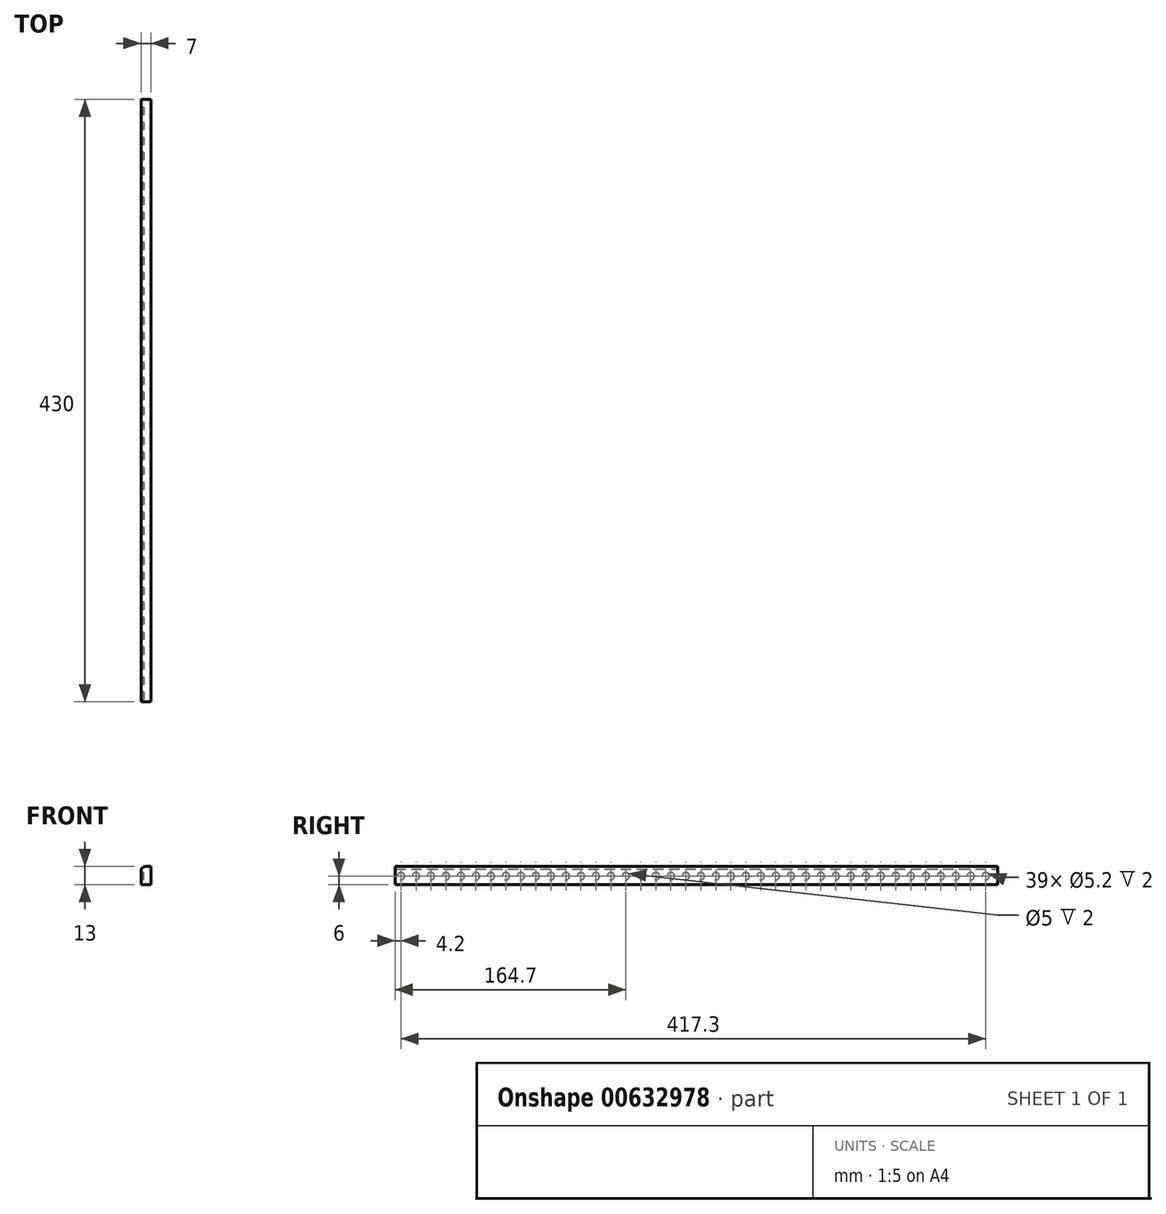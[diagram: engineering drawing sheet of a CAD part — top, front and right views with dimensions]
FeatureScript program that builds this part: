
annotation { "Feature Type Name" : "Feature", "Feature Type Description" : "" }
export const myFeature = defineFeature(function(context is Context, id is Id, definition is map)
    precondition{}
    {
        {
            var Q0;
            Q0=qCreatedBy(makeId("Right.planeOp"),FACE);
            var sketch = newSketch(context, id + "F0", { "sketchPlane" : qUnion([Q0])});
            skLineSegment(sketch, "E0.bottom", {"start": v(215, 7) * mm, "end": v(-215, 7) * mm});
            skLineSegment(sketch, "E0.top", {"start": v(215, -6) * mm, "end": v(-215, -6) * mm});
            skLineSegment(sketch, "E0.left", {"start": v(215, 7) * mm, "end": v(215, -6) * mm});
            skLineSegment(sketch, "E0.right", {"start": v(-215, 7) * mm, "end": v(-215, -6) * mm});
            skLineSegment(sketch, "E1", {"start": v(215, 0) * mm, "end": v(-215, 0) * mm, "construction": true});
            skCircle(sketch, "E2", {"center": v(206.5, 0) * mm, "radius": 2.6 * mm});
            skCircle(sketch, "E3", {"center": v(195.8, 0) * mm, "radius": 2.6 * mm});
            skCircle(sketch, "E4", {"center": v(185.1, 0) * mm, "radius": 2.6 * mm});
            skCircle(sketch, "E5", {"center": v(174.4, 0) * mm, "radius": 2.6 * mm});
            skCircle(sketch, "E6", {"center": v(163.7, 0) * mm, "radius": 2.6 * mm});
            skCircle(sketch, "E7", {"center": v(153, 0) * mm, "radius": 2.6 * mm});
            skCircle(sketch, "E8", {"center": v(142.3, 0) * mm, "radius": 2.6 * mm});
            skCircle(sketch, "E9", {"center": v(131.6, 0) * mm, "radius": 2.6 * mm});
            skCircle(sketch, "E10", {"center": v(120.9, 0) * mm, "radius": 2.6 * mm});
            skCircle(sketch, "E11", {"center": v(110.2, 0) * mm, "radius": 2.6 * mm});
            skCircle(sketch, "E12", {"center": v(99.5, 0) * mm, "radius": 2.6 * mm});
            skCircle(sketch, "E13", {"center": v(88.8, 0) * mm, "radius": 2.6 * mm});
            skCircle(sketch, "E14", {"center": v(78.1, 0) * mm, "radius": 2.6 * mm});
            skCircle(sketch, "E15", {"center": v(67.4, 0) * mm, "radius": 2.6 * mm});
            skCircle(sketch, "E16", {"center": v(56.7, 0) * mm, "radius": 2.6 * mm});
            skCircle(sketch, "E17", {"center": v(46, 0) * mm, "radius": 2.6 * mm});
            skCircle(sketch, "E18", {"center": v(35.3, 0) * mm, "radius": 2.6 * mm});
            skCircle(sketch, "E19", {"center": v(24.6, 0) * mm, "radius": 2.6 * mm});
            skCircle(sketch, "E20", {"center": v(13.9, 0) * mm, "radius": 2.6 * mm});
            skCircle(sketch, "E21", {"center": v(3.2, 0) * mm, "radius": 2.6 * mm});
            skCircle(sketch, "E22", {"center": v(-7.5, 0) * mm, "radius": 2.6 * mm});
            skCircle(sketch, "E23", {"center": v(-18.2, 0) * mm, "radius": 2.6 * mm});
            skCircle(sketch, "E24", {"center": v(-28.9, 0) * mm, "radius": 2.6 * mm});
            skCircle(sketch, "E25", {"center": v(-39.6, 0) * mm, "radius": 2.6 * mm});
            skCircle(sketch, "E26", {"center": v(-50.3, 0) * mm, "radius": 2.5 * mm});
            skCircle(sketch, "E27", {"center": v(-61, 0) * mm, "radius": 2.6 * mm});
            skCircle(sketch, "E28", {"center": v(-71.7, 0) * mm, "radius": 2.6 * mm});
            skCircle(sketch, "E29", {"center": v(-82.4, 0) * mm, "radius": 2.6 * mm});
            skCircle(sketch, "E30", {"center": v(-93.1, 0) * mm, "radius": 2.6 * mm});
            skCircle(sketch, "E31", {"center": v(-103.8, 0) * mm, "radius": 2.6 * mm});
            skCircle(sketch, "E32", {"center": v(-114.5, 0) * mm, "radius": 2.6 * mm});
            skCircle(sketch, "E33", {"center": v(-125.2, 0) * mm, "radius": 2.6 * mm});
            skCircle(sketch, "E34", {"center": v(-135.9, 0) * mm, "radius": 2.6 * mm});
            skCircle(sketch, "E35", {"center": v(-146.6, 0) * mm, "radius": 2.6 * mm});
            skCircle(sketch, "E36", {"center": v(-157.3, 0) * mm, "radius": 2.6 * mm});
            skCircle(sketch, "E37", {"center": v(-168, 0) * mm, "radius": 2.6 * mm});
            skCircle(sketch, "E38", {"center": v(-178.7, 0) * mm, "radius": 2.6 * mm});
            skCircle(sketch, "E39", {"center": v(-189.4, 0) * mm, "radius": 2.6 * mm});
            skCircle(sketch, "E40", {"center": v(-200.1, 0) * mm, "radius": 2.6 * mm});
            skCircle(sketch, "E41", {"center": v(-210.8, 0) * mm, "radius": 2.6 * mm});
            skSolve(sketch);
        }
        {
            var Q0;
            Q0=makeQuery(id+"F0.imprint","IMPRINT",FACE,{"disambiguationData":[TD([[makeQuery(id+"F0.imprint","IMPRINT",EDGE,{"derivedFrom":sQuery(id+"F0.wireOp",EDGE,"E0.bottom")}),1.0]])]});
            var Q1;
            Q1=makeQuery(id+"F0.imprint","IMPRINT",FACE,{"disambiguationData":[TD([[makeQuery(id+"F0.imprint","IMPRINT",EDGE,{"derivedFrom":sQuery(id+"F0.wireOp",EDGE,"E34")}),1.0]])]});
            var Q2;
            Q2=makeQuery(id+"F0.imprint","IMPRINT",FACE,{"disambiguationData":[TD([[makeQuery(id+"F0.imprint","IMPRINT",EDGE,{"derivedFrom":sQuery(id+"F0.wireOp",EDGE,"E18")}),1.0]])]});
            var Q3;
            Q3=makeQuery(id+"F0.imprint","IMPRINT",FACE,{"disambiguationData":[TD([[makeQuery(id+"F0.imprint","IMPRINT",EDGE,{"derivedFrom":sQuery(id+"F0.wireOp",EDGE,"E16")}),1.0]])]});
            var Q4;
            Q4=makeQuery(id+"F0.imprint","IMPRINT",FACE,{"disambiguationData":[TD([[makeQuery(id+"F0.imprint","IMPRINT",EDGE,{"derivedFrom":sQuery(id+"F0.wireOp",EDGE,"E15")}),1.0]])]});
            var Q5;
            Q5=makeQuery(id+"F0.imprint","IMPRINT",FACE,{"disambiguationData":[TD([[makeQuery(id+"F0.imprint","IMPRINT",EDGE,{"derivedFrom":sQuery(id+"F0.wireOp",EDGE,"E33")}),1.0]])]});
            var Q6;
            Q6=makeQuery(id+"F0.imprint","IMPRINT",FACE,{"disambiguationData":[TD([[makeQuery(id+"F0.imprint","IMPRINT",EDGE,{"derivedFrom":sQuery(id+"F0.wireOp",EDGE,"E38")}),1.0]])]});
            var Q7;
            Q7=makeQuery(id+"F0.imprint","IMPRINT",FACE,{"disambiguationData":[TD([[makeQuery(id+"F0.imprint","IMPRINT",EDGE,{"derivedFrom":sQuery(id+"F0.wireOp",EDGE,"E31")}),1.0]])]});
            var Q8;
            Q8=makeQuery(id+"F0.imprint","IMPRINT",FACE,{"disambiguationData":[TD([[makeQuery(id+"F0.imprint","IMPRINT",EDGE,{"derivedFrom":sQuery(id+"F0.wireOp",EDGE,"E17")}),1.0]])]});
            var Q9;
            Q9=makeQuery(id+"F0.imprint","IMPRINT",FACE,{"disambiguationData":[TD([[makeQuery(id+"F0.imprint","IMPRINT",EDGE,{"derivedFrom":sQuery(id+"F0.wireOp",EDGE,"E36")}),1.0]])]});
            var Q10;
            Q10=makeQuery(id+"F0.imprint","IMPRINT",FACE,{"disambiguationData":[TD([[makeQuery(id+"F0.imprint","IMPRINT",EDGE,{"derivedFrom":sQuery(id+"F0.wireOp",EDGE,"E22")}),1.0]])]});
            var Q11;
            Q11=makeQuery(id+"F0.imprint","IMPRINT",FACE,{"disambiguationData":[TD([[makeQuery(id+"F0.imprint","IMPRINT",EDGE,{"derivedFrom":sQuery(id+"F0.wireOp",EDGE,"E20")}),1.0]])]});
            var Q12;
            Q12=makeQuery(id+"F0.imprint","IMPRINT",FACE,{"disambiguationData":[TD([[makeQuery(id+"F0.imprint","IMPRINT",EDGE,{"derivedFrom":sQuery(id+"F0.wireOp",EDGE,"E24")}),1.0]])]});
            var Q13;
            Q13=makeQuery(id+"F0.imprint","IMPRINT",FACE,{"disambiguationData":[TD([[makeQuery(id+"F0.imprint","IMPRINT",EDGE,{"derivedFrom":sQuery(id+"F0.wireOp",EDGE,"E40")}),1.0]])]});
            var Q14;
            Q14=makeQuery(id+"F0.imprint","IMPRINT",FACE,{"disambiguationData":[TD([[makeQuery(id+"F0.imprint","IMPRINT",EDGE,{"derivedFrom":sQuery(id+"F0.wireOp",EDGE,"E26")}),1.0]])]});
            var Q15;
            Q15=makeQuery(id+"F0.imprint","IMPRINT",FACE,{"disambiguationData":[TD([[makeQuery(id+"F0.imprint","IMPRINT",EDGE,{"derivedFrom":sQuery(id+"F0.wireOp",EDGE,"E30")}),1.0]])]});
            var Q16;
            Q16=makeQuery(id+"F0.imprint","IMPRINT",FACE,{"disambiguationData":[TD([[makeQuery(id+"F0.imprint","IMPRINT",EDGE,{"derivedFrom":sQuery(id+"F0.wireOp",EDGE,"E35")}),1.0]])]});
            var Q17;
            Q17=makeQuery(id+"F0.imprint","IMPRINT",FACE,{"disambiguationData":[TD([[makeQuery(id+"F0.imprint","IMPRINT",EDGE,{"derivedFrom":sQuery(id+"F0.wireOp",EDGE,"E19")}),1.0]])]});
            var Q18;
            Q18=makeQuery(id+"F0.imprint","IMPRINT",FACE,{"disambiguationData":[TD([[makeQuery(id+"F0.imprint","IMPRINT",EDGE,{"derivedFrom":sQuery(id+"F0.wireOp",EDGE,"E39")}),1.0]])]});
            var Q19;
            Q19=makeQuery(id+"F0.imprint","IMPRINT",FACE,{"disambiguationData":[TD([[makeQuery(id+"F0.imprint","IMPRINT",EDGE,{"derivedFrom":sQuery(id+"F0.wireOp",EDGE,"E32")}),1.0]])]});
            var Q20;
            Q20=makeQuery(id+"F0.imprint","IMPRINT",FACE,{"disambiguationData":[TD([[makeQuery(id+"F0.imprint","IMPRINT",EDGE,{"derivedFrom":sQuery(id+"F0.wireOp",EDGE,"E23")}),1.0]])]});
            var Q21;
            Q21=makeQuery(id+"F0.imprint","IMPRINT",FACE,{"disambiguationData":[TD([[makeQuery(id+"F0.imprint","IMPRINT",EDGE,{"derivedFrom":sQuery(id+"F0.wireOp",EDGE,"E25")}),1.0]])]});
            var Q22;
            Q22=makeQuery(id+"F0.imprint","IMPRINT",FACE,{"disambiguationData":[TD([[makeQuery(id+"F0.imprint","IMPRINT",EDGE,{"derivedFrom":sQuery(id+"F0.wireOp",EDGE,"E29")}),1.0]])]});
            var Q23;
            Q23=makeQuery(id+"F0.imprint","IMPRINT",FACE,{"disambiguationData":[TD([[makeQuery(id+"F0.imprint","IMPRINT",EDGE,{"derivedFrom":sQuery(id+"F0.wireOp",EDGE,"E14")}),1.0]])]});
            var Q24;
            Q24=makeQuery(id+"F0.imprint","IMPRINT",FACE,{"disambiguationData":[TD([[makeQuery(id+"F0.imprint","IMPRINT",EDGE,{"derivedFrom":sQuery(id+"F0.wireOp",EDGE,"E13")}),1.0]])]});
            var Q25;
            Q25=makeQuery(id+"F0.imprint","IMPRINT",FACE,{"disambiguationData":[TD([[makeQuery(id+"F0.imprint","IMPRINT",EDGE,{"derivedFrom":sQuery(id+"F0.wireOp",EDGE,"E12")}),1.0]])]});
            var Q26;
            Q26=makeQuery(id+"F0.imprint","IMPRINT",FACE,{"disambiguationData":[TD([[makeQuery(id+"F0.imprint","IMPRINT",EDGE,{"derivedFrom":sQuery(id+"F0.wireOp",EDGE,"E11")}),1.0]])]});
            var Q27;
            Q27=makeQuery(id+"F0.imprint","IMPRINT",FACE,{"disambiguationData":[TD([[makeQuery(id+"F0.imprint","IMPRINT",EDGE,{"derivedFrom":sQuery(id+"F0.wireOp",EDGE,"E10")}),1.0]])]});
            var Q28;
            Q28=makeQuery(id+"F0.imprint","IMPRINT",FACE,{"disambiguationData":[TD([[makeQuery(id+"F0.imprint","IMPRINT",EDGE,{"derivedFrom":sQuery(id+"F0.wireOp",EDGE,"E9")}),1.0]])]});
            var Q29;
            Q29=makeQuery(id+"F0.imprint","IMPRINT",FACE,{"disambiguationData":[TD([[makeQuery(id+"F0.imprint","IMPRINT",EDGE,{"derivedFrom":sQuery(id+"F0.wireOp",EDGE,"E8")}),1.0]])]});
            var Q30;
            Q30=makeQuery(id+"F0.imprint","IMPRINT",FACE,{"disambiguationData":[TD([[makeQuery(id+"F0.imprint","IMPRINT",EDGE,{"derivedFrom":sQuery(id+"F0.wireOp",EDGE,"E28")}),1.0]])]});
            var Q31;
            Q31=makeQuery(id+"F0.imprint","IMPRINT",FACE,{"disambiguationData":[TD([[makeQuery(id+"F0.imprint","IMPRINT",EDGE,{"derivedFrom":sQuery(id+"F0.wireOp",EDGE,"E7")}),1.0]])]});
            var Q32;
            Q32=makeQuery(id+"F0.imprint","IMPRINT",FACE,{"disambiguationData":[TD([[makeQuery(id+"F0.imprint","IMPRINT",EDGE,{"derivedFrom":sQuery(id+"F0.wireOp",EDGE,"E6")}),1.0]])]});
            var Q33;
            Q33=makeQuery(id+"F0.imprint","IMPRINT",FACE,{"disambiguationData":[TD([[makeQuery(id+"F0.imprint","IMPRINT",EDGE,{"derivedFrom":sQuery(id+"F0.wireOp",EDGE,"E5")}),1.0]])]});
            var Q34;
            Q34=makeQuery(id+"F0.imprint","IMPRINT",FACE,{"disambiguationData":[TD([[makeQuery(id+"F0.imprint","IMPRINT",EDGE,{"derivedFrom":sQuery(id+"F0.wireOp",EDGE,"E4")}),1.0]])]});
            var Q35;
            Q35=makeQuery(id+"F0.imprint","IMPRINT",FACE,{"disambiguationData":[TD([[makeQuery(id+"F0.imprint","IMPRINT",EDGE,{"derivedFrom":sQuery(id+"F0.wireOp",EDGE,"E37")}),1.0]])]});
            var Q36;
            Q36=makeQuery(id+"F0.imprint","IMPRINT",FACE,{"disambiguationData":[TD([[makeQuery(id+"F0.imprint","IMPRINT",EDGE,{"derivedFrom":sQuery(id+"F0.wireOp",EDGE,"E21")}),1.0]])]});
            var Q37;
            Q37=makeQuery(id+"F0.imprint","IMPRINT",FACE,{"disambiguationData":[TD([[makeQuery(id+"F0.imprint","IMPRINT",EDGE,{"derivedFrom":sQuery(id+"F0.wireOp",EDGE,"E3")}),1.0]])]});
            var Q38;
            Q38=makeQuery(id+"F0.imprint","IMPRINT",FACE,{"disambiguationData":[TD([[makeQuery(id+"F0.imprint","IMPRINT",EDGE,{"derivedFrom":sQuery(id+"F0.wireOp",EDGE,"E2")}),1.0]])]});
            var Q39;
            Q39=makeQuery(id+"F0.imprint","IMPRINT",FACE,{"disambiguationData":[TD([[makeQuery(id+"F0.imprint","IMPRINT",EDGE,{"derivedFrom":sQuery(id+"F0.wireOp",EDGE,"E27")}),1.0]])]});
            var Q40;
            Q40=makeQuery(id+"F0.imprint","IMPRINT",FACE,{"disambiguationData":[TD([[makeQuery(id+"F0.imprint","IMPRINT",EDGE,{"derivedFrom":sQuery(id+"F0.wireOp",EDGE,"E41")}),1.0]])]});
            extrude(context, id + "F1", {"entities" : qUnion([Q0, Q1, Q2, Q3, Q4, Q5, Q6, Q7, Q8, Q9, Q10, Q11, Q12, Q13, Q14, Q15, Q16, Q17, Q18, Q19, Q20, Q21, Q22, Q23, Q24, Q25, Q26, Q27, Q28, Q29, Q30, Q31, Q32, Q33, Q34, Q35, Q36, Q37, Q38, Q39, Q40]), "depth" : 7 * mm, "offsetDistance" : 25 * mm});
        }
        {
            var Q0;
            Q0=makeQuery(id+"F0.imprint","IMPRINT",FACE,{"disambiguationData":[TD([[makeQuery(id+"F0.imprint","IMPRINT",EDGE,{"derivedFrom":sQuery(id+"F0.wireOp",EDGE,"E2")}),1.0]])]});
            var Q1;
            Q1=makeQuery(id+"F0.imprint","IMPRINT",FACE,{"disambiguationData":[TD([[makeQuery(id+"F0.imprint","IMPRINT",EDGE,{"derivedFrom":sQuery(id+"F0.wireOp",EDGE,"E3")}),1.0]])]});
            var Q2;
            Q2=makeQuery(id+"F0.imprint","IMPRINT",FACE,{"disambiguationData":[TD([[makeQuery(id+"F0.imprint","IMPRINT",EDGE,{"derivedFrom":sQuery(id+"F0.wireOp",EDGE,"E4")}),1.0]])]});
            var Q3;
            Q3=makeQuery(id+"F0.imprint","IMPRINT",FACE,{"disambiguationData":[TD([[makeQuery(id+"F0.imprint","IMPRINT",EDGE,{"derivedFrom":sQuery(id+"F0.wireOp",EDGE,"E5")}),1.0]])]});
            var Q4;
            Q4=makeQuery(id+"F0.imprint","IMPRINT",FACE,{"disambiguationData":[TD([[makeQuery(id+"F0.imprint","IMPRINT",EDGE,{"derivedFrom":sQuery(id+"F0.wireOp",EDGE,"E6")}),1.0]])]});
            var Q5;
            Q5=makeQuery(id+"F0.imprint","IMPRINT",FACE,{"disambiguationData":[TD([[makeQuery(id+"F0.imprint","IMPRINT",EDGE,{"derivedFrom":sQuery(id+"F0.wireOp",EDGE,"E7")}),1.0]])]});
            var Q6;
            Q6=makeQuery(id+"F0.imprint","IMPRINT",FACE,{"disambiguationData":[TD([[makeQuery(id+"F0.imprint","IMPRINT",EDGE,{"derivedFrom":sQuery(id+"F0.wireOp",EDGE,"E8")}),1.0]])]});
            var Q7;
            Q7=makeQuery(id+"F0.imprint","IMPRINT",FACE,{"disambiguationData":[TD([[makeQuery(id+"F0.imprint","IMPRINT",EDGE,{"derivedFrom":sQuery(id+"F0.wireOp",EDGE,"E9")}),1.0]])]});
            var Q8;
            Q8=makeQuery(id+"F0.imprint","IMPRINT",FACE,{"disambiguationData":[TD([[makeQuery(id+"F0.imprint","IMPRINT",EDGE,{"derivedFrom":sQuery(id+"F0.wireOp",EDGE,"E10")}),1.0]])]});
            var Q9;
            Q9=makeQuery(id+"F0.imprint","IMPRINT",FACE,{"disambiguationData":[TD([[makeQuery(id+"F0.imprint","IMPRINT",EDGE,{"derivedFrom":sQuery(id+"F0.wireOp",EDGE,"E11")}),1.0]])]});
            var Q10;
            Q10=makeQuery(id+"F0.imprint","IMPRINT",FACE,{"disambiguationData":[TD([[makeQuery(id+"F0.imprint","IMPRINT",EDGE,{"derivedFrom":sQuery(id+"F0.wireOp",EDGE,"E12")}),1.0]])]});
            var Q11;
            Q11=makeQuery(id+"F0.imprint","IMPRINT",FACE,{"disambiguationData":[TD([[makeQuery(id+"F0.imprint","IMPRINT",EDGE,{"derivedFrom":sQuery(id+"F0.wireOp",EDGE,"E13")}),1.0]])]});
            var Q12;
            Q12=makeQuery(id+"F0.imprint","IMPRINT",FACE,{"disambiguationData":[TD([[makeQuery(id+"F0.imprint","IMPRINT",EDGE,{"derivedFrom":sQuery(id+"F0.wireOp",EDGE,"E14")}),1.0]])]});
            var Q13;
            Q13=makeQuery(id+"F0.imprint","IMPRINT",FACE,{"disambiguationData":[TD([[makeQuery(id+"F0.imprint","IMPRINT",EDGE,{"derivedFrom":sQuery(id+"F0.wireOp",EDGE,"E15")}),1.0]])]});
            var Q14;
            Q14=makeQuery(id+"F0.imprint","IMPRINT",FACE,{"disambiguationData":[TD([[makeQuery(id+"F0.imprint","IMPRINT",EDGE,{"derivedFrom":sQuery(id+"F0.wireOp",EDGE,"E16")}),1.0]])]});
            var Q15;
            Q15=makeQuery(id+"F0.imprint","IMPRINT",FACE,{"disambiguationData":[TD([[makeQuery(id+"F0.imprint","IMPRINT",EDGE,{"derivedFrom":sQuery(id+"F0.wireOp",EDGE,"E17")}),1.0]])]});
            var Q16;
            Q16=makeQuery(id+"F0.imprint","IMPRINT",FACE,{"disambiguationData":[TD([[makeQuery(id+"F0.imprint","IMPRINT",EDGE,{"derivedFrom":sQuery(id+"F0.wireOp",EDGE,"E18")}),1.0]])]});
            var Q17;
            Q17=makeQuery(id+"F0.imprint","IMPRINT",FACE,{"disambiguationData":[TD([[makeQuery(id+"F0.imprint","IMPRINT",EDGE,{"derivedFrom":sQuery(id+"F0.wireOp",EDGE,"E19")}),1.0]])]});
            var Q18;
            Q18=makeQuery(id+"F0.imprint","IMPRINT",FACE,{"disambiguationData":[TD([[makeQuery(id+"F0.imprint","IMPRINT",EDGE,{"derivedFrom":sQuery(id+"F0.wireOp",EDGE,"E20")}),1.0]])]});
            var Q19;
            Q19=makeQuery(id+"F0.imprint","IMPRINT",FACE,{"disambiguationData":[TD([[makeQuery(id+"F0.imprint","IMPRINT",EDGE,{"derivedFrom":sQuery(id+"F0.wireOp",EDGE,"E21")}),1.0]])]});
            var Q20;
            Q20=makeQuery(id+"F0.imprint","IMPRINT",FACE,{"disambiguationData":[TD([[makeQuery(id+"F0.imprint","IMPRINT",EDGE,{"derivedFrom":sQuery(id+"F0.wireOp",EDGE,"E22")}),1.0]])]});
            var Q21;
            Q21=makeQuery(id+"F0.imprint","IMPRINT",FACE,{"disambiguationData":[TD([[makeQuery(id+"F0.imprint","IMPRINT",EDGE,{"derivedFrom":sQuery(id+"F0.wireOp",EDGE,"E23")}),1.0]])]});
            var Q22;
            Q22=makeQuery(id+"F0.imprint","IMPRINT",FACE,{"disambiguationData":[TD([[makeQuery(id+"F0.imprint","IMPRINT",EDGE,{"derivedFrom":sQuery(id+"F0.wireOp",EDGE,"E24")}),1.0]])]});
            var Q23;
            Q23=makeQuery(id+"F0.imprint","IMPRINT",FACE,{"disambiguationData":[TD([[makeQuery(id+"F0.imprint","IMPRINT",EDGE,{"derivedFrom":sQuery(id+"F0.wireOp",EDGE,"E25")}),1.0]])]});
            var Q24;
            Q24=makeQuery(id+"F0.imprint","IMPRINT",FACE,{"disambiguationData":[TD([[makeQuery(id+"F0.imprint","IMPRINT",EDGE,{"derivedFrom":sQuery(id+"F0.wireOp",EDGE,"E26")}),1.0]])]});
            var Q25;
            Q25=makeQuery(id+"F0.imprint","IMPRINT",FACE,{"disambiguationData":[TD([[makeQuery(id+"F0.imprint","IMPRINT",EDGE,{"derivedFrom":sQuery(id+"F0.wireOp",EDGE,"E27")}),1.0]])]});
            var Q26;
            Q26=makeQuery(id+"F0.imprint","IMPRINT",FACE,{"disambiguationData":[TD([[makeQuery(id+"F0.imprint","IMPRINT",EDGE,{"derivedFrom":sQuery(id+"F0.wireOp",EDGE,"E28")}),1.0]])]});
            var Q27;
            Q27=makeQuery(id+"F0.imprint","IMPRINT",FACE,{"disambiguationData":[TD([[makeQuery(id+"F0.imprint","IMPRINT",EDGE,{"derivedFrom":sQuery(id+"F0.wireOp",EDGE,"E29")}),1.0]])]});
            var Q28;
            Q28=makeQuery(id+"F0.imprint","IMPRINT",FACE,{"disambiguationData":[TD([[makeQuery(id+"F0.imprint","IMPRINT",EDGE,{"derivedFrom":sQuery(id+"F0.wireOp",EDGE,"E30")}),1.0]])]});
            var Q29;
            Q29=makeQuery(id+"F0.imprint","IMPRINT",FACE,{"disambiguationData":[TD([[makeQuery(id+"F0.imprint","IMPRINT",EDGE,{"derivedFrom":sQuery(id+"F0.wireOp",EDGE,"E31")}),1.0]])]});
            var Q30;
            Q30=makeQuery(id+"F0.imprint","IMPRINT",FACE,{"disambiguationData":[TD([[makeQuery(id+"F0.imprint","IMPRINT",EDGE,{"derivedFrom":sQuery(id+"F0.wireOp",EDGE,"E32")}),1.0]])]});
            var Q31;
            Q31=makeQuery(id+"F0.imprint","IMPRINT",FACE,{"disambiguationData":[TD([[makeQuery(id+"F0.imprint","IMPRINT",EDGE,{"derivedFrom":sQuery(id+"F0.wireOp",EDGE,"E33")}),1.0]])]});
            var Q32;
            Q32=makeQuery(id+"F0.imprint","IMPRINT",FACE,{"disambiguationData":[TD([[makeQuery(id+"F0.imprint","IMPRINT",EDGE,{"derivedFrom":sQuery(id+"F0.wireOp",EDGE,"E34")}),1.0]])]});
            var Q33;
            Q33=makeQuery(id+"F0.imprint","IMPRINT",FACE,{"disambiguationData":[TD([[makeQuery(id+"F0.imprint","IMPRINT",EDGE,{"derivedFrom":sQuery(id+"F0.wireOp",EDGE,"E35")}),1.0]])]});
            var Q34;
            Q34=makeQuery(id+"F0.imprint","IMPRINT",FACE,{"disambiguationData":[TD([[makeQuery(id+"F0.imprint","IMPRINT",EDGE,{"derivedFrom":sQuery(id+"F0.wireOp",EDGE,"E36")}),1.0]])]});
            var Q35;
            Q35=makeQuery(id+"F0.imprint","IMPRINT",FACE,{"disambiguationData":[TD([[makeQuery(id+"F0.imprint","IMPRINT",EDGE,{"derivedFrom":sQuery(id+"F0.wireOp",EDGE,"E38")}),1.0]])]});
            var Q36;
            Q36=makeQuery(id+"F0.imprint","IMPRINT",FACE,{"disambiguationData":[TD([[makeQuery(id+"F0.imprint","IMPRINT",EDGE,{"derivedFrom":sQuery(id+"F0.wireOp",EDGE,"E39")}),1.0]])]});
            var Q37;
            Q37=makeQuery(id+"F0.imprint","IMPRINT",FACE,{"disambiguationData":[TD([[makeQuery(id+"F0.imprint","IMPRINT",EDGE,{"derivedFrom":sQuery(id+"F0.wireOp",EDGE,"E40")}),1.0]])]});
            var Q38;
            Q38=makeQuery(id+"F0.imprint","IMPRINT",FACE,{"disambiguationData":[TD([[makeQuery(id+"F0.imprint","IMPRINT",EDGE,{"derivedFrom":sQuery(id+"F0.wireOp",EDGE,"E41")}),1.0]])]});
            var Q39;
            Q39=makeQuery(id+"F0.imprint","IMPRINT",FACE,{"disambiguationData":[TD([[makeQuery(id+"F0.imprint","IMPRINT",EDGE,{"derivedFrom":sQuery(id+"F0.wireOp",EDGE,"E37")}),1.0]])]});
            extrude(context, id + "F2", {"entities" : qUnion([Q0, Q1, Q2, Q3, Q4, Q5, Q6, Q7, Q8, Q9, Q10, Q11, Q12, Q13, Q14, Q15, Q16, Q17, Q18, Q19, Q20, Q21, Q22, Q23, Q24, Q25, Q26, Q27, Q28, Q29, Q30, Q31, Q32, Q33, Q34, Q35, Q36, Q37, Q38, Q39]), "operationType" : NewBodyOperationType.REMOVE, "depth" : 2 * mm, "offsetDistance" : 25 * mm});
        }
        {
            var Q0;
            Q0=makeQuery(id+"F1.opExtrude","CAP_EDGE",EDGE,{"disambiguationData":[OSD([sQuery(id+"F0.wireOp",EDGE,"E0.bottom")])],"isStart":true});
            chamfer(context, id + "F3", {"entities" : qUnion([Q0]), "width" : 2 * mm, "tangentPropagation" : true});
        }
        {
            var Q0;
            {var subQ0=sQuery(id+"F0.wireOp",EDGE,"E0.bottom");Q0=makeQuery(id+"F3.opChamfer","BLEND_EDGE",EDGE,{"blendedFrom":[makeQuery(id+"F1.opExtrude","CAP_EDGE",EDGE,{"disambiguationData":[OSD([subQ0])],"isStart":true}),makeQuery(id+"F1.opExtrude","SWEPT_FACE",FACE,{"disambiguationData":[OSD([subQ0])]})],"blendedInto":[makeQuery(id+"F1.opExtrude","SWEPT_FACE",FACE,{"disambiguationData":[OSD([subQ0])]})]});}
            fillet(context, id + "F4", {"entities" : qUnion([Q0]), "radius" : 5 * mm, "tangentPropagation" : true, "allowEdgeOverflow" : false});
        }
    });
